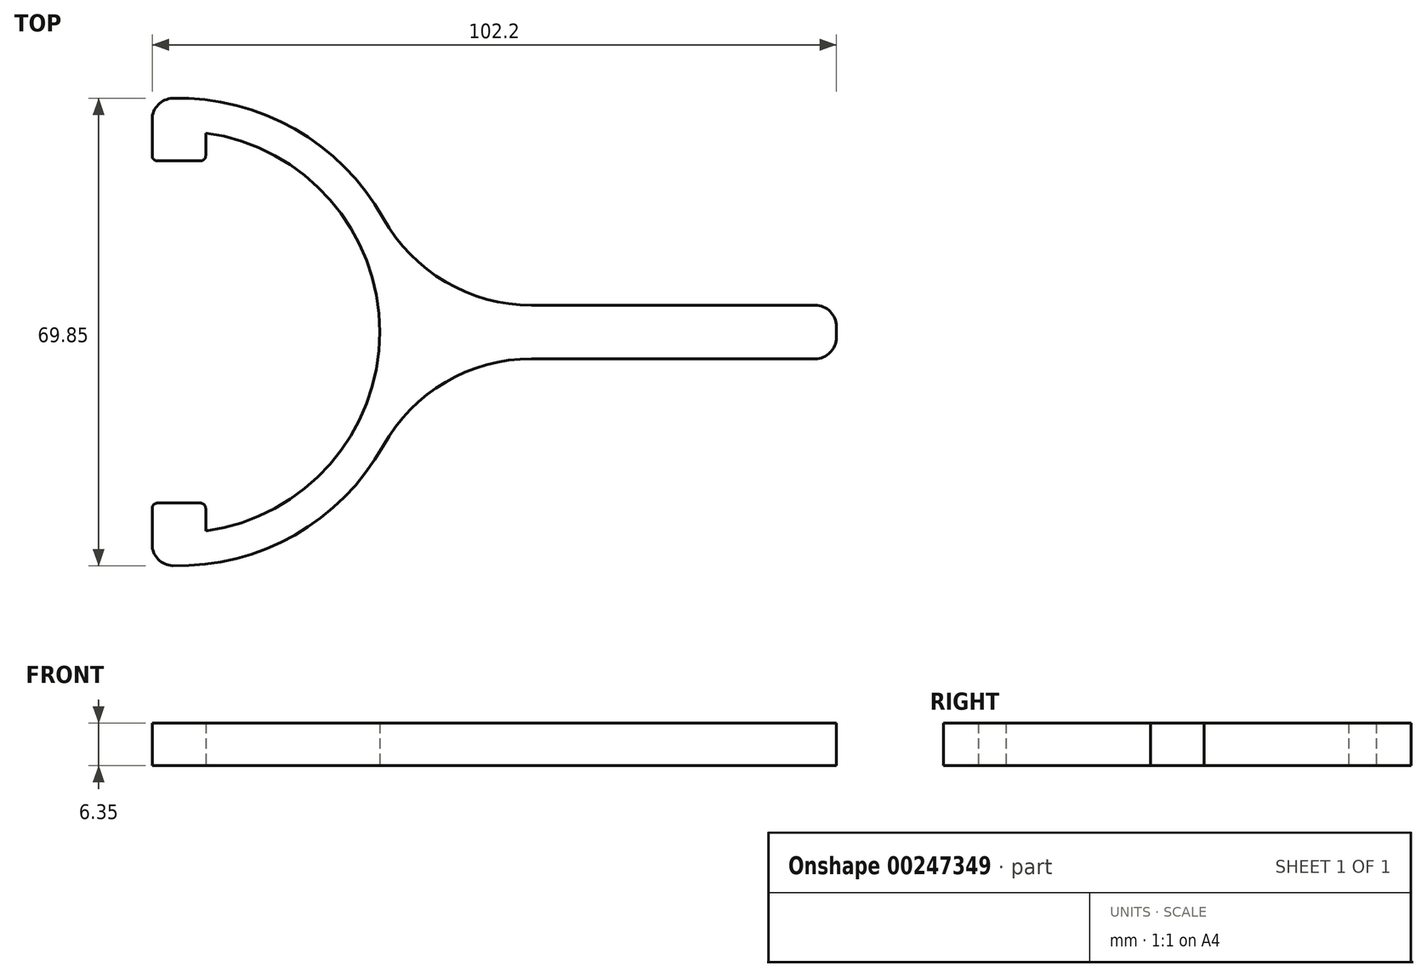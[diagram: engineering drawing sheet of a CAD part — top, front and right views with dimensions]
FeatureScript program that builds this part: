
annotation { "Feature Type Name" : "Feature", "Feature Type Description" : "" }
export const myFeature = defineFeature(function(context is Context, id is Id, definition is map)
    precondition{}
    {
        {
            var Q0;
            Q0=qCreatedBy(makeId("Top.planeOp"),FACE);
            var sketch = newSketch(context, id + "F0", { "sketchPlane" : qUnion([Q0])});
            skLineSegment(sketch, "E0", {"start": v(-28.9, 0) * mm, "end": v(28.9, 0) * mm, "construction": true});
            skLineSegment(sketch, "E1", {"start": v(0, -25.1) * mm, "end": v(0, 25.1) * mm, "construction": true});
            skLineSegment(sketch, "E2.bottom", {"start": v(-28.62, -4) * mm, "end": v(-24.78, -4) * mm});
            skLineSegment(sketch, "E2.top", {"start": v(-28.62, 4) * mm, "end": v(-24.78, 4) * mm});
            skLineSegment(sketch, "E2.left", {"start": v(-28.62, -4) * mm, "end": v(-28.62, 4) * mm, "construction": true});
            skLineSegment(sketch, "E2.right", {"start": v(28.62, -4) * mm, "end": v(28.62, 4) * mm, "construction": true});
            skPoint(sketch, "E2.middle", {"position": v(0, 0) * mm});
            skLineSegment(sketch, "E3.left", {"start": v(-4, 28.62) * mm, "end": v(-4, 24.78) * mm});
            skLineSegment(sketch, "E3.right", {"start": v(4, 28.62) * mm, "end": v(4, 24.78) * mm});
            skLineSegment(sketch, "E4", {"start": v(4, 24.78) * mm, "end": v(4, -24.78) * mm, "construction": true});
            skLineSegment(sketch, "E5", {"start": v(-4, 24.78) * mm, "end": v(-4, -24.78) * mm, "construction": true});
            skLineSegment(sketch, "E6", {"start": v(24.78, 4) * mm, "end": v(28.62, 4) * mm});
            skLineSegment(sketch, "E7", {"start": v(24.78, -4) * mm, "end": v(28.62, -4) * mm});
            skLineSegment(sketch, "E8", {"start": v(-24.83, 4) * mm, "end": v(-24.78, 4) * mm, "construction": true});
            skLineSegment(sketch, "E9", {"start": v(-24.78, -4) * mm, "end": v(24.78, -4) * mm, "construction": true});
            skLineSegment(sketch, "E10", {"start": v(-4, -24.78) * mm, "end": v(-4, -28.62) * mm});
            skLineSegment(sketch, "E11", {"start": v(4, -24.78) * mm, "end": v(4, -28.62) * mm});
            skArc(sketch, "E12", {"start": v(-4, 28.62) * mm, "mid": v(-20.44, 20.44) * mm, "end": v(-28.62, 4) * mm});
            skArc(sketch, "E13", {"start": v(28.62, 4) * mm, "mid": v(20.44, 20.44) * mm, "end": v(4, 28.62) * mm});
            skArc(sketch, "E14", {"start": v(28.62, -4) * mm, "mid": v(28.9, 0) * mm, "end": v(28.62, 4) * mm});
            skArc(sketch, "E15", {"start": v(4, -28.62) * mm, "mid": v(20.44, -20.44) * mm, "end": v(28.62, -4) * mm});
            skArc(sketch, "E16", {"start": v(-28.62, -4) * mm, "mid": v(-20.44, -20.44) * mm, "end": v(-4, -28.62) * mm});
            skArc(sketch, "E17", {"start": v(-28.62, 4) * mm, "mid": v(-28.9, 0) * mm, "end": v(-28.62, -4) * mm});
            skLineSegment(sketch, "E18", {"start": v(-4, 24.78) * mm, "end": v(-4, 24.78) * mm});
            skArc(sketch, "E19", {"start": v(4, 24.78) * mm, "mid": v(0, 25.1) * mm, "end": v(-4, 24.78) * mm});
            skArc(sketch, "E20", {"start": v(24.78, 4) * mm, "mid": v(17.75, 17.75) * mm, "end": v(4, 24.78) * mm, "construction": true});
            skArc(sketch, "E21", {"start": v(24.78, -4) * mm, "mid": v(25.1, 0) * mm, "end": v(24.78, 4) * mm});
            skArc(sketch, "E22", {"start": v(4, -24.78) * mm, "mid": v(17.75, -17.75) * mm, "end": v(24.78, -4) * mm, "construction": true});
            skArc(sketch, "E23", {"start": v(-4, -24.78) * mm, "mid": v(0, -25.1) * mm, "end": v(4, -24.78) * mm});
            skArc(sketch, "E24", {"start": v(-24.78, -4) * mm, "mid": v(-17.75, -17.75) * mm, "end": v(-4, -24.78) * mm, "construction": true});
            skLineSegment(sketch, "E25", {"start": v(-24.83, 4) * mm, "end": v(24.78, 4) * mm, "construction": true});
            skArc(sketch, "E26", {"start": v(-24.78, 4) * mm, "mid": v(-25.1, 0) * mm, "end": v(-24.78, -4) * mm});
            skArc(sketch, "E27", {"start": v(-4, 24.78) * mm, "mid": v(-17.75, 17.75) * mm, "end": v(-24.78, 4) * mm, "construction": true});
            skCircle(sketch, "E28", {"center": v(0, 0) * mm, "radius": 18.25 * mm});
            skSolve(sketch);
        }
        {
            var Q0;
            Q0=makeQuery(id+"F0.imprint","IMPRINT",FACE,{"disambiguationData":[TD([[makeQuery(id+"F0.imprint","IMPRINT",EDGE,{"derivedFrom":sQuery(id+"F0.wireOp",EDGE,"E2.bottom")}),-1.0]])]});
            extrude(context, id + "F1", {"entities" : qUnion([Q0]), "depth" : 11 * mm});
        }
        {
            var Q0;
            Q0=makeQuery(id+"F1.opExtrude","CAP_FACE",FACE,{"disambiguationData":[OSD([sQuery(id+"F0.wireOp",EDGE,"E2.bottom"),sQuery(id+"F0.wireOp",EDGE,"E2.top"),sQuery(id+"F0.wireOp",EDGE,"E3.left"),sQuery(id+"F0.wireOp",EDGE,"E3.right"),sQuery(id+"F0.wireOp",EDGE,"E6"),sQuery(id+"F0.wireOp",EDGE,"E7"),sQuery(id+"F0.wireOp",EDGE,"E10"),sQuery(id+"F0.wireOp",EDGE,"E11"),sQuery(id+"F0.wireOp",EDGE,"E12"),sQuery(id+"F0.wireOp",EDGE,"E13"),sQuery(id+"F0.wireOp",EDGE,"E15"),sQuery(id+"F0.wireOp",EDGE,"E16"),sQuery(id+"F0.wireOp",EDGE,"E19"),sQuery(id+"F0.wireOp",EDGE,"E21"),sQuery(id+"F0.wireOp",EDGE,"E23"),sQuery(id+"F0.wireOp",EDGE,"E26"),sQuery(id+"F0.wireOp",EDGE,"E28")])],"isStart":false});
            var sketch = newSketch(context, id + "F2", { "sketchPlane" : qUnion([Q0])});
            skPoint(sketch, "E29.oppositeSnap0", {"position": v(4, -26.7) * mm});
            skArc(sketch, "E30", {"start": v(-4, -34.7) * mm, "mid": v(15.93, -31.08) * mm, "end": v(30.5, -17.02) * mm});
            skPoint(sketch, "E31.firstSnap0", {"position": v(-4, -26.7) * mm});
            skLineSegment(sketch, "E31.bottom", {"start": v(-4, -34.7) * mm, "end": v(4, -34.7) * mm, "construction": true});
            skLineSegment(sketch, "E31.top", {"start": v(-4, -25.57) * mm, "end": v(4, -25.57) * mm});
            skLineSegment(sketch, "E31.left", {"start": v(-4, -34.7) * mm, "end": v(-4, -25.57) * mm});
            skLineSegment(sketch, "E31.right", {"start": v(4, -29.73) * mm, "end": v(4, -25.57) * mm});
            skLineSegment(sketch, "E32", {"start": v(-34.93, 0) * mm, "end": v(34.93, 0) * mm, "construction": true});
            skPoint(sketch, "E32.startSnap0", {"position": v(-25.1, 0) * mm});
            skPoint(sketch, "E32.endSnap0", {"position": v(25.1, 0) * mm});
            skLineSegment(sketch, "E33.MirrorCS", {"start": v(-4, 25.57) * mm, "end": v(4, 25.57) * mm});
            skLineSegment(sketch, "E34.MirrorCS", {"start": v(4, 29.73) * mm, "end": v(4, 25.57) * mm});
            skLineSegment(sketch, "E35.MirrorCS", {"start": v(-4, 34.7) * mm, "end": v(-4, 25.57) * mm});
            skLineSegment(sketch, "E36.bottom", {"start": v(52.68, 4) * mm, "end": v(98.2, 4) * mm});
            skLineSegment(sketch, "E36.top", {"start": v(52.68, -4) * mm, "end": v(98.2, -4) * mm});
            skLineSegment(sketch, "E36.left", {"start": v(34.7, 4) * mm, "end": v(34.7, -4) * mm, "construction": true});
            skLineSegment(sketch, "E36.right", {"start": v(98.2, 4) * mm, "end": v(98.2, -4) * mm});
            skArc(sketch, "E37", {"start": v(30.5, 17.02) * mm, "mid": v(15.93, 31.08) * mm, "end": v(-4, 34.7) * mm});
            skPoint(sketch, "E38.visualSharp", {"position": v(34.7, 4) * mm});
            skArc(sketch, "E38.filletArc", {"start": v(30.5, 17.02) * mm, "mid": v(39.82, 7.5) * mm, "end": v(52.68, 4) * mm});
            skPoint(sketch, "E39.visualSharp", {"position": v(34.7, -4) * mm});
            skArc(sketch, "E39.filletArc", {"start": v(52.68, -4) * mm, "mid": v(39.82, -7.5) * mm, "end": v(30.5, -17.02) * mm});
            skArc(sketch, "E40", {"start": v(4, -29.73) * mm, "mid": v(30, 0) * mm, "end": v(4, 29.73) * mm});
            skPoint(sketch, "E41.orphan", {"position": v(4, 34.7) * mm});
            skSolve(sketch);
        }
        {
            var Q0;
            {var subQ9=sQuery(id+"F2.wireOp",EDGE,"E30");Q0=makeQuery(id+"F2.imprint","IMPRINT",FACE,{"disambiguationData":[TD([[makeQuery(id+"F2.imprint","IMPRINT",EDGE,{"derivedFrom":subQ9}),1.0]])]});}
            extrude(context, id + "F3", {"entities" : qUnion([Q0]), "depth" : 6.35 * mm});
        }
        {
            var Q0;
            Q0=makeQuery(id+"F3.opExtrude","SWEPT_EDGE",EDGE,{"disambiguationData":[OSD([sQuery(id+"F2.wireOp",EDGE,"E30"),sQuery(id+"F2.wireOp",EDGE,"E31.left")])]});
            var Q1;
            Q1=makeQuery(id+"F3.opExtrude","SWEPT_EDGE",EDGE,{"disambiguationData":[OSD([sQuery(id+"F2.wireOp",EDGE,"E35.MirrorCS"),sQuery(id+"F2.wireOp",EDGE,"E37")])]});
            var Q2;
            Q2=makeQuery(id+"F3.opExtrude","SWEPT_EDGE",EDGE,{"disambiguationData":[OSD([sQuery(id+"F2.wireOp",EDGE,"E36.top"),sQuery(id+"F2.wireOp",EDGE,"E36.right")])]});
            var Q3;
            Q3=makeQuery(id+"F3.opExtrude","SWEPT_EDGE",EDGE,{"disambiguationData":[OSD([sQuery(id+"F2.wireOp",EDGE,"E36.bottom"),sQuery(id+"F2.wireOp",EDGE,"E36.right")])]});
            fillet(context, id + "F4", {"entities" : qUnion([Q0, Q1, Q2, Q3]), "radius" : 3.17 * mm, "tangentPropagation" : true, "allowEdgeOverflow" : false});
        }
        {
            var Q0;
            Q0=makeQuery(id+"F3.opExtrude","SWEPT_EDGE",EDGE,{"disambiguationData":[OSD([sQuery(id+"F0.wireOp",EDGE,"E10"),sQuery(id+"F2.wireOp",EDGE,"E31.top"),sQuery(id+"F2.wireOp",EDGE,"E31.left")])]});
            var Q1;
            Q1=makeQuery(id+"F3.opExtrude","SWEPT_EDGE",EDGE,{"disambiguationData":[OSD([sQuery(id+"F0.wireOp",EDGE,"E11"),sQuery(id+"F2.wireOp",EDGE,"E31.top"),sQuery(id+"F2.wireOp",EDGE,"E31.right")])]});
            var Q2;
            Q2=makeQuery(id+"F3.opExtrude","SWEPT_EDGE",EDGE,{"disambiguationData":[OSD([sQuery(id+"F0.wireOp",EDGE,"E3.left"),sQuery(id+"F2.wireOp",EDGE,"E33.MirrorCS"),sQuery(id+"F2.wireOp",EDGE,"E35.MirrorCS")])]});
            var Q3;
            Q3=makeQuery(id+"F3.opExtrude","SWEPT_EDGE",EDGE,{"disambiguationData":[OSD([sQuery(id+"F0.wireOp",EDGE,"E3.right"),sQuery(id+"F2.wireOp",EDGE,"E33.MirrorCS"),sQuery(id+"F2.wireOp",EDGE,"E34.MirrorCS")])]});
            fillet(context, id + "F5", {"entities" : qUnion([Q0, Q1, Q2, Q3]), "radius" : 0.8 * mm, "tangentPropagation" : true, "allowEdgeOverflow" : false});
        }
        {
            var Q0;
            Q0=makeQuery(id+"F1.opExtrude","SWEPT_BODY",BODY,{"disambiguationData":[OSD([sQuery(id+"F0.wireOp",EDGE,"E2.bottom"),sQuery(id+"F0.wireOp",EDGE,"E2.top"),sQuery(id+"F0.wireOp",EDGE,"E3.left"),sQuery(id+"F0.wireOp",EDGE,"E3.right"),sQuery(id+"F0.wireOp",EDGE,"E6"),sQuery(id+"F0.wireOp",EDGE,"E7"),sQuery(id+"F0.wireOp",EDGE,"E10"),sQuery(id+"F0.wireOp",EDGE,"E11"),sQuery(id+"F0.wireOp",EDGE,"E12"),sQuery(id+"F0.wireOp",EDGE,"E13"),sQuery(id+"F0.wireOp",EDGE,"E15"),sQuery(id+"F0.wireOp",EDGE,"E16"),sQuery(id+"F0.wireOp",EDGE,"E19"),sQuery(id+"F0.wireOp",EDGE,"E21"),sQuery(id+"F0.wireOp",EDGE,"E23"),sQuery(id+"F0.wireOp",EDGE,"E26"),sQuery(id+"F0.wireOp",EDGE,"E28")])]});
            deleteBodies(context, id + "F6", {"entities" : qUnion([Q0])});
        }
    });
